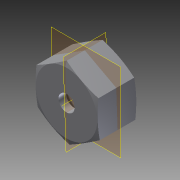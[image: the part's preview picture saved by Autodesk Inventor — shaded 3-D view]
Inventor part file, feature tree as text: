
AUTODESK INVENTOR PART (.ipt)
format: ipt  version: 2016 SP1 (Build 200210100, 210)  size: 136,704 bytes
history: native  units: in
note: dims shown in document units (in); Inventor stores cm internally (conversion verified against a paired STEP export)
features: sketch x4, plane x3, extrude x3, reference x2, thread x1, other x1, revolve x1, mirror x1
ambient origin geometry x8: Origin, YZ Plane, XZ Plane, XY Plane, X Axis, Y Axis, Z Axis, Center Point
bodies: Body1 (feature_tree)
feature tree (16):
  plane  "Work Plane3"
  extrude  "Extrusion2"  Depth=0.5in
  extrude  "Extrusion3"  Depth=0.375in TaperAngle=0.0deg
  extrude  "Extrusion4"  TaperAngle=90.0deg  [1 undecoded]
  thread  "Thread1"  [1 undecoded]
  plane  "Work Plane4"
  other  "Work Axis4"
  revolve  "Revolution2"  [1 undecoded]
  plane  "Work Plane5"
  mirror  "Mirror1"
  sketch  "Sketch6"  dims[d3=0.3125in d4=0.0in d5=0.5in]
  sketch  "Sketch7"  dims[d6=0.25in d7=-0.0123in d8=0.375in d9=0.0in]
  reference  "Reference1"
  sketch  "Sketch8"  dims[d10=0.392in d11=0.0in d12=90.0deg d13=0.045in]
  reference  "Reference2"
  sketch  "Sketch9"
note: 3 required parameter values undecoded (feature->parameter linkage not recoverable at this tier; creation-order binding heuristic only, values carry confidence <= 0.55)
